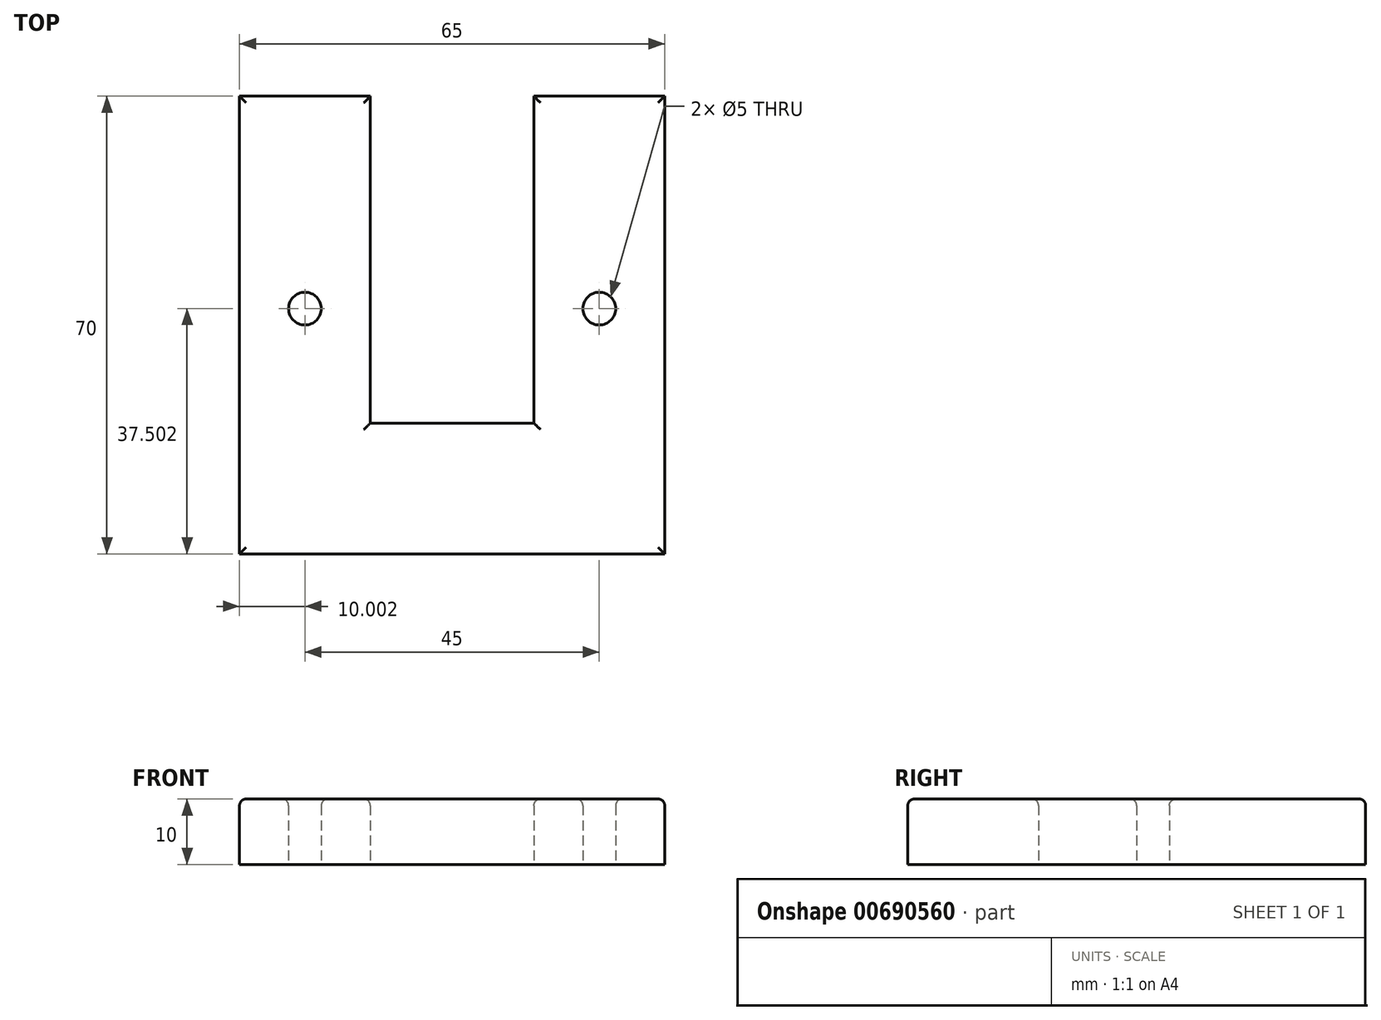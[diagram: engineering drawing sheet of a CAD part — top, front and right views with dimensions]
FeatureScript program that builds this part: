
annotation { "Feature Type Name" : "Feature", "Feature Type Description" : "" }
export const myFeature = defineFeature(function(context is Context, id is Id, definition is map)
    precondition{}
    {
        {
            var Q0;
            Q0=qCreatedBy(makeId("Top.planeOp"),FACE);
            var sketch = newSketch(context, id + "F0", { "sketchPlane" : qUnion([Q0])});
            skLineSegment(sketch, "E0", {"start": v(-24.78, 51.35) * mm, "end": v(-24.78, -18.65) * mm});
            skLineSegment(sketch, "E1", {"start": v(-24.78, -18.65) * mm, "end": v(40.22, -18.65) * mm});
            skLineSegment(sketch, "E2", {"start": v(40.22, -18.65) * mm, "end": v(40.22, 51.35) * mm});
            skLineSegment(sketch, "E3", {"start": v(40.22, 51.35) * mm, "end": v(20.22, 51.35) * mm});
            skLineSegment(sketch, "E4", {"start": v(20.22, 51.35) * mm, "end": v(20.22, 1.35) * mm});
            skLineSegment(sketch, "E5", {"start": v(20.22, 1.35) * mm, "end": v(-4.78, 1.35) * mm});
            skLineSegment(sketch, "E6", {"start": v(-4.78, 1.35) * mm, "end": v(-4.78, 51.35) * mm});
            skLineSegment(sketch, "E7", {"start": v(-4.78, 51.35) * mm, "end": v(-24.78, 51.35) * mm});
            skCircle(sketch, "E8", {"center": v(-14.78, 18.85) * mm, "radius": 2.5 * mm});
            skCircle(sketch, "E9", {"center": v(30.22, 18.85) * mm, "radius": 2.5 * mm});
            skSolve(sketch);
        }
        {
            var Q0;
            Q0 = qSketchRegion(id + "F0", true);
            extrude(context, id + "F1", {"entities" : qUnion([Q0]), "depth" : 10 * mm, "offsetDistance" : 25 * mm});
        }
        {
            var Q0;
            Q0 = qSketchRegion(id + "F0", true);
            extrude(context, id + "F2", {"entities" : qUnion([Q0]), "operationType" : NewBodyOperationType.ADD, "depth" : 10 * mm, "offsetDistance" : 25 * mm});
        }
        {
            var Q0;
            Q0=makeQuery(id+"F1.opExtrude","CAP_FACE",FACE,{"disambiguationData":[OSD([sQuery(id+"F0.wireOp",EDGE,"E0"),sQuery(id+"F0.wireOp",EDGE,"E1"),sQuery(id+"F0.wireOp",EDGE,"E2"),sQuery(id+"F0.wireOp",EDGE,"E3"),sQuery(id+"F0.wireOp",EDGE,"E4"),sQuery(id+"F0.wireOp",EDGE,"E5"),sQuery(id+"F0.wireOp",EDGE,"E6"),sQuery(id+"F0.wireOp",EDGE,"E7"),sQuery(id+"F0.wireOp",EDGE,"E8"),sQuery(id+"F0.wireOp",EDGE,"E9")])],"isStart":false});
            fillet(context, id + "F3", {"entities" : qUnion([Q0]), "radius" : 1 * mm, "tangentPropagation" : true, "allowEdgeOverflow" : false});
        }
    });
